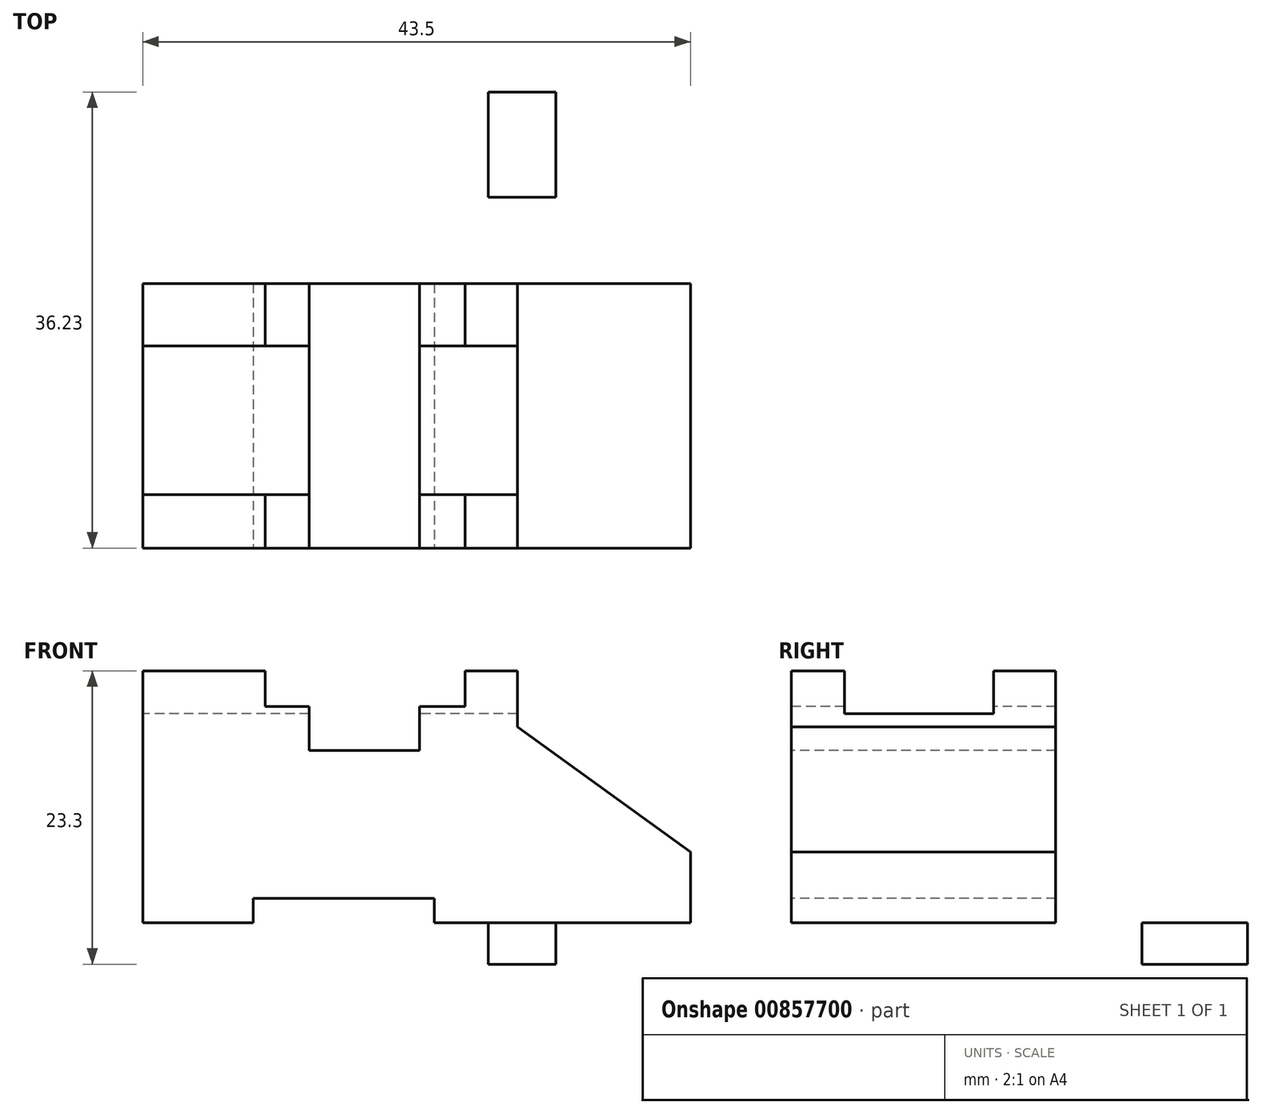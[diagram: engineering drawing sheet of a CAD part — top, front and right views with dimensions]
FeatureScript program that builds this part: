
annotation { "Feature Type Name" : "Feature", "Feature Type Description" : "" }
export const myFeature = defineFeature(function(context is Context, id is Id, definition is map)
    precondition{}
    {
        {
            var Q0;
            Q0=qCreatedBy(makeId("Front.planeOp"),FACE);
            var sketch = newSketch(context, id + "F0", { "sketchPlane" : qUnion([Q0])});
            skLineSegment(sketch, "E0.bottom", {"start": v(0, 0) * mm, "end": v(43.5, 0) * mm});
            skLineSegment(sketch, "E0.top", {"start": v(0, 20) * mm, "end": v(43.5, 20) * mm});
            skLineSegment(sketch, "E0.left", {"start": v(0, 0) * mm, "end": v(0, 20) * mm});
            skLineSegment(sketch, "E0.right", {"start": v(43.5, 0) * mm, "end": v(43.5, 20) * mm});
            skSolve(sketch);
        }
        {
            var Q0;
            Q0=makeQuery(id+"F0.imprint","IMPRINT",FACE,{"disambiguationData":[TD([[makeQuery(id+"F0.imprint","IMPRINT",EDGE,{"derivedFrom":sQuery(id+"F0.wireOp",EDGE,"E0.bottom")}),1.0]])]});
            extrude(context, id + "F1", {"entities" : qUnion([Q0]), "depth" : 21 * mm, "offsetDistance" : 25 * mm});
        }
        {
            var Q0;
            Q0=qCreatedBy(makeId("Front.planeOp"),FACE);
            var sketch = newSketch(context, id + "F2", { "sketchPlane" : qUnion([Q0])});
            skLineSegment(sketch, "E1.bottom", {"start": v(4.12, 0) * mm, "end": v(27.62, 0) * mm});
            skLineSegment(sketch, "E1.top", {"start": v(4.12, 2) * mm, "end": v(27.62, 2) * mm});
            skLineSegment(sketch, "E1.left", {"start": v(4.12, 0) * mm, "end": v(4.12, 2) * mm});
            skLineSegment(sketch, "E1.right", {"start": v(27.62, 0) * mm, "end": v(27.62, 2) * mm});
            skSolve(sketch);
        }
        {
            var Q0;
            Q0=makeQuery(id+"F2.imprint","IMPRINT",FACE,{"disambiguationData":[TD([[makeQuery(id+"F2.imprint","IMPRINT",EDGE,{"derivedFrom":sQuery(id+"F2.wireOp",EDGE,"E1.bottom")}),1.0]])]});
            extrude(context, id + "F3", {"entities" : qUnion([Q0]), "operationType" : NewBodyOperationType.REMOVE, "endBound" : BoundingType.THROUGH_ALL, "oppositeDirection" : true, "depth" : 25 * mm, "offsetDistance" : 25 * mm});
        }
        {
            var Q0;
            Q0=makeQuery(id+"F1.opExtrude","CAP_FACE",FACE,{"disambiguationData":[OSD([sQuery(id+"F0.wireOp",EDGE,"E0.bottom"),sQuery(id+"F0.wireOp",EDGE,"E0.top"),sQuery(id+"F0.wireOp",EDGE,"E0.left"),sQuery(id+"F0.wireOp",EDGE,"E0.right")])],"isStart":false});
            var sketch = newSketch(context, id + "F4", { "sketchPlane" : qUnion([Q0])});
            skLineSegment(sketch, "E2.bottom", {"start": v(9.74, 20) * mm, "end": v(25.59, 20) * mm});
            skLineSegment(sketch, "E2.top", {"start": v(9.74, 17.16) * mm, "end": v(25.59, 17.16) * mm});
            skLineSegment(sketch, "E2.left", {"start": v(9.74, 20) * mm, "end": v(9.74, 17.16) * mm});
            skLineSegment(sketch, "E2.right", {"start": v(25.59, 20) * mm, "end": v(25.59, 17.16) * mm});
            skLineSegment(sketch, "E3.bottom", {"start": v(13.22, 17.16) * mm, "end": v(21.97, 17.16) * mm});
            skLineSegment(sketch, "E3.top", {"start": v(13.22, 13.68) * mm, "end": v(21.97, 13.68) * mm});
            skLineSegment(sketch, "E3.left", {"start": v(13.22, 17.16) * mm, "end": v(13.22, 13.68) * mm});
            skLineSegment(sketch, "E3.right", {"start": v(21.97, 17.16) * mm, "end": v(21.97, 13.68) * mm});
            skLineSegment(sketch, "E4.bottom", {"start": v(8.77, 0) * mm, "end": v(23.16, 0) * mm});
            skLineSegment(sketch, "E4.top", {"start": v(8.77, 1.93) * mm, "end": v(23.16, 1.93) * mm});
            skLineSegment(sketch, "E4.left", {"start": v(8.77, 0) * mm, "end": v(8.77, 1.93) * mm});
            skLineSegment(sketch, "E4.right", {"start": v(23.16, 0) * mm, "end": v(23.16, 1.93) * mm});
            skLineSegment(sketch, "E5", {"start": v(29.76, 20) * mm, "end": v(29.76, 15.56) * mm});
            skLineSegment(sketch, "E6", {"start": v(29.76, 15.56) * mm, "end": v(43.5, 5.62) * mm});
            skSolve(sketch);
        }
        {
            var Q0;
            Q0 = qSketchRegion(id + "F4", true);
            var Q1;
            {var subQ0=sQuery(id+"F4.wireOp",EDGE,"E5");Q1=makeQuery(id+"F4.imprint","IMPRINT",FACE,{"disambiguationData":[TD([[makeQuery(id+"F4.imprint","IMPRINT",EDGE,{"derivedFrom":subQ0}),1.0]])]});}
            extrude(context, id + "F5", {"entities" : qUnion([Q0, Q1]), "operationType" : NewBodyOperationType.REMOVE, "endBound" : BoundingType.THROUGH_ALL, "oppositeDirection" : true, "depth" : 25 * mm, "offsetDistance" : 25 * mm});
        }
        {
            var Q0;
            Q0=qCreatedBy(makeId("Top.planeOp"),FACE);
            var sketch = newSketch(context, id + "F6", { "sketchPlane" : qUnion([Q0])});
            skLineSegment(sketch, "E7.bottom", {"start": v(47.92, -4.94) * mm, "end": v(29.86, -4.94) * mm});
            skLineSegment(sketch, "E7.top", {"start": v(47.92, -16.01) * mm, "end": v(29.86, -16.01) * mm});
            skLineSegment(sketch, "E7.left", {"start": v(47.92, -4.94) * mm, "end": v(47.92, -16.01) * mm});
            skLineSegment(sketch, "E7.right", {"start": v(29.86, -4.94) * mm, "end": v(29.86, -16.01) * mm});
            skSolve(sketch);
        }
        {
            var Q0;
            Q0=makeQuery(id+"F6.imprint","IMPRINT",FACE,{"disambiguationData":[TD([[makeQuery(id+"F6.imprint","IMPRINT",EDGE,{"derivedFrom":sQuery(id+"F6.wireOp",EDGE,"E7.bottom")}),1.0]])]});
            extrude(context, id + "F7", {"entities" : qUnion([Q0]), "operationType" : NewBodyOperationType.REMOVE, "endBound" : BoundingType.THROUGH_ALL, "depth" : 25 * mm, "offsetDistance" : 25 * mm});
        }
        {
            var Q0;
            Q0=makeQuery(id+"F1.opExtrude","SWEPT_FACE",FACE,{"disambiguationData":[OSD([sQuery(id+"F0.wireOp",EDGE,"E0.left")])]});
            var sketch = newSketch(context, id + "F8", { "sketchPlane" : qUnion([Q0])});
            skLineSegment(sketch, "E8.bottom", {"start": v(4.94, 20) * mm, "end": v(16.77, 20) * mm});
            skLineSegment(sketch, "E8.top", {"start": v(4.94, 16.58) * mm, "end": v(16.77, 16.58) * mm});
            skLineSegment(sketch, "E8.left", {"start": v(4.94, 20) * mm, "end": v(4.94, 16.58) * mm});
            skLineSegment(sketch, "E8.right", {"start": v(16.77, 20) * mm, "end": v(16.77, 16.58) * mm});
            skLineSegment(sketch, "E9.bottom", {"start": v(6.86, 16.58) * mm, "end": v(15.23, 16.58) * mm});
            skLineSegment(sketch, "E9.top", {"start": v(6.86, 13.36) * mm, "end": v(15.23, 13.36) * mm});
            skLineSegment(sketch, "E9.left", {"start": v(6.86, 16.58) * mm, "end": v(6.86, 13.36) * mm});
            skLineSegment(sketch, "E9.right", {"start": v(15.23, 16.58) * mm, "end": v(15.23, 13.36) * mm});
            skSolve(sketch);
        }
        {
            var Q0;
            Q0=makeQuery(id+"F8.imprint","IMPRINT",FACE,{"disambiguationData":[TD([[makeQuery(id+"F8.imprint","IMPRINT",EDGE,{"derivedFrom":sQuery(id+"F8.wireOp",EDGE,"E9.bottom")}),-1.0]])]});
            var Q1;
            Q1=makeQuery(id+"F8.imprint","IMPRINT",FACE,{"disambiguationData":[TD([[makeQuery(id+"F8.imprint","IMPRINT",EDGE,{"derivedFrom":sQuery(id+"F8.wireOp",EDGE,"E8.bottom")}),1.0]])]});
            extrude(context, id + "F9", {"entities" : qUnion([Q0, Q1]), "operationType" : NewBodyOperationType.REMOVE, "endBound" : BoundingType.THROUGH_ALL, "oppositeDirection" : true, "depth" : 25 * mm, "offsetDistance" : 25 * mm});
        }
        {
            var Q0;
            Q0=makeQuery(id+"F7.boolean.opBoolean","COPY",FACE,{"derivedFrom":makeQuery(id+"F7.opExtrude","SWEPT_FACE",FACE,{"disambiguationData":[OSD([sQuery(id+"F6.wireOp",EDGE,"E7.right")])]})});
            extrude(context, id + "F10", {"entities" : qUnion([Q0]), "operationType" : NewBodyOperationType.ADD, "depth" : 13.8 * mm, "offsetDistance" : 25 * mm});
        }
        {
            var Q0;
            Q0=makeQuery(id+"F10.opExtrude","SWEPT_FACE",FACE,{"disambiguationData":[OSD([sQuery(id+"F6.wireOp",EDGE,"E7.top"),sQuery(id+"F6.wireOp",EDGE,"E7.right")])]});
            extrude(context, id + "F11", {"entities" : qUnion([Q0]), "operationType" : NewBodyOperationType.REMOVE, "endBound" : BoundingType.THROUGH_ALL, "oppositeDirection" : true, "depth" : 25 * mm, "offsetDistance" : 25 * mm});
        }
        {
            var Q0;
            {var subQ0=sQuery(id+"F8.wireOp",EDGE,"E9.top");Q0=makeQuery(id+"F10.boolean.opBoolean","MERGE",FACE,{"derivedFrom":[makeQuery(id+"F9.boolean.opBoolean","COPY",FACE,{"derivedFrom":makeQuery(id+"F9.opExtrude","SWEPT_FACE",FACE,{"disambiguationData":[OSD([subQ0])]})}),makeQuery(id+"F10.opExtrude","SWEPT_FACE",FACE,{"disambiguationData":[OSD([sQuery(id+"F6.wireOp",EDGE,"E7.right"),subQ0])]})]});}
            var sketch = newSketch(context, id + "F12", { "sketchPlane" : qUnion([Q0])});
            skLineSegment(sketch, "E10.bottom", {"start": v(27.44, -6.86) * mm, "end": v(32.8, -6.86) * mm});
            skLineSegment(sketch, "E10.top", {"start": v(27.44, -15.23) * mm, "end": v(32.8, -15.23) * mm});
            skLineSegment(sketch, "E10.left", {"start": v(27.44, -6.86) * mm, "end": v(27.44, -15.23) * mm});
            skLineSegment(sketch, "E10.right", {"start": v(32.8, -6.86) * mm, "end": v(32.8, -15.23) * mm});
            skSolve(sketch);
        }
        {
            var Q0;
            Q0 = qSketchRegion(id + "F12", true);
            extrude(context, id + "F13", {"entities" : qUnion([Q0]), "operationType" : NewBodyOperationType.ADD, "depth" : 3.3 * mm, "offsetDistance" : 25 * mm});
        }
    });
